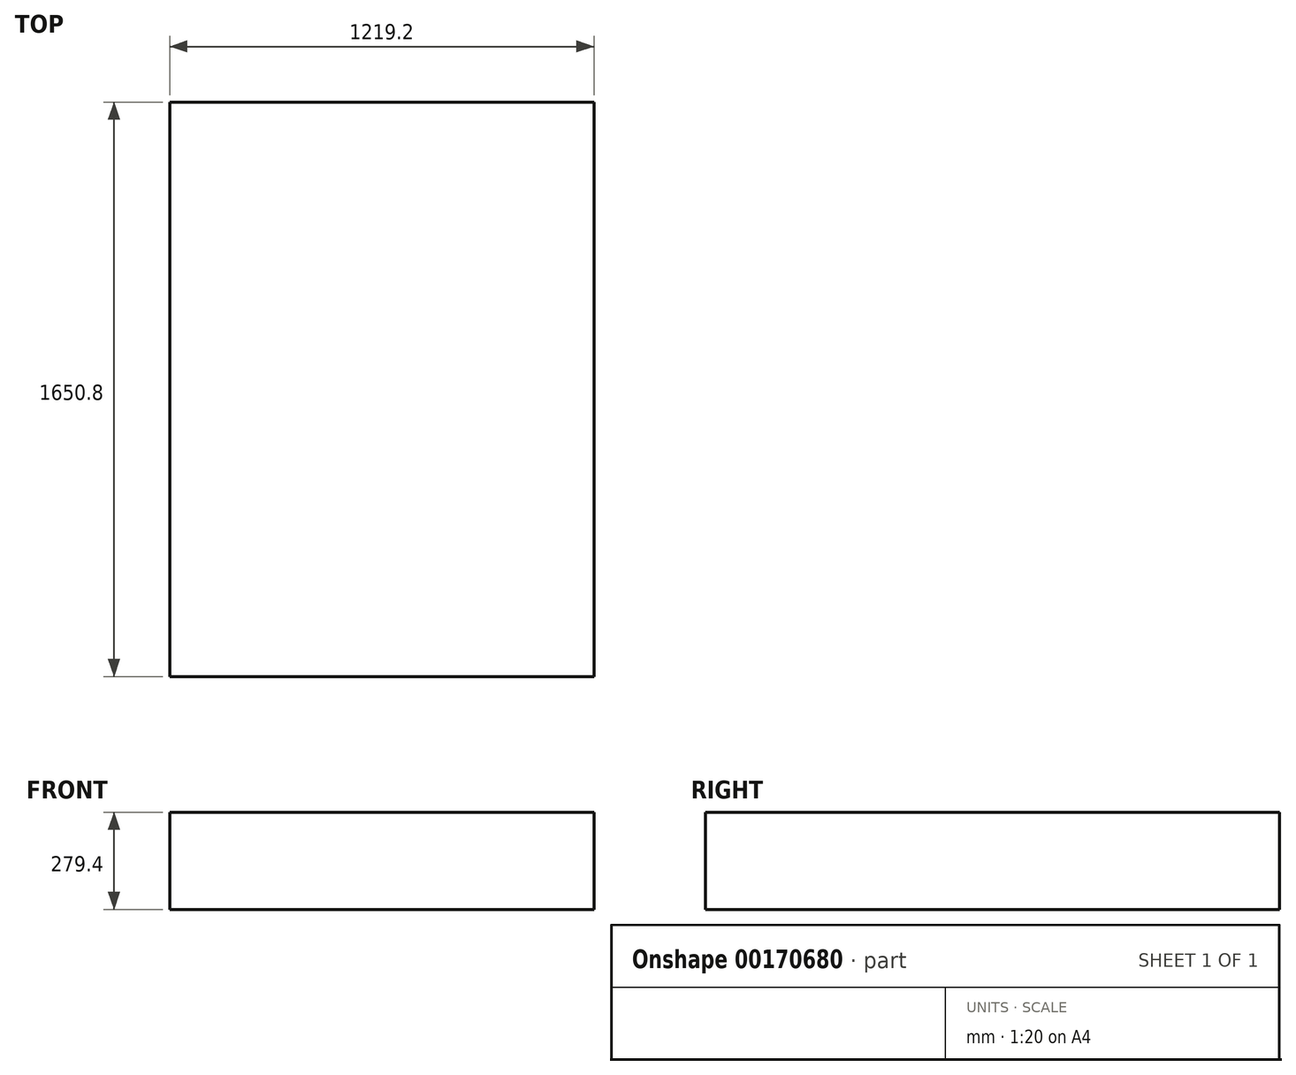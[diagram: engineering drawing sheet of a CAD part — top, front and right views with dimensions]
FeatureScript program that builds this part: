
annotation { "Feature Type Name" : "Feature", "Feature Type Description" : "" }
export const myFeature = defineFeature(function(context is Context, id is Id, definition is map)
    precondition{}
    {
        {
            var Q0;
            Q0=qCreatedBy(makeId("Front.planeOp"),FACE);
            var sketch = newSketch(context, id + "F0", { "sketchPlane" : qUnion([Q0])});
            skLineSegment(sketch, "E0.bottom", {"start": v(0, 0) * mm, "end": v(1219.2, 0) * mm});
            skLineSegment(sketch, "E0.top", {"start": v(0, 279.4) * mm, "end": v(1219.2, 279.4) * mm});
            skLineSegment(sketch, "E0.left", {"start": v(0, 0) * mm, "end": v(0, 279.4) * mm});
            skLineSegment(sketch, "E0.right", {"start": v(1219.2, 0) * mm, "end": v(1219.2, 279.4) * mm});
            skSolve(sketch);
        }
        {
            var Q0;
            Q0 = qSketchRegion(id + "F0", true);
            extrude(context, id + "F1", {"entities" : qUnion([Q0]), "depth" : 1650.8 * mm});
        }
    });
